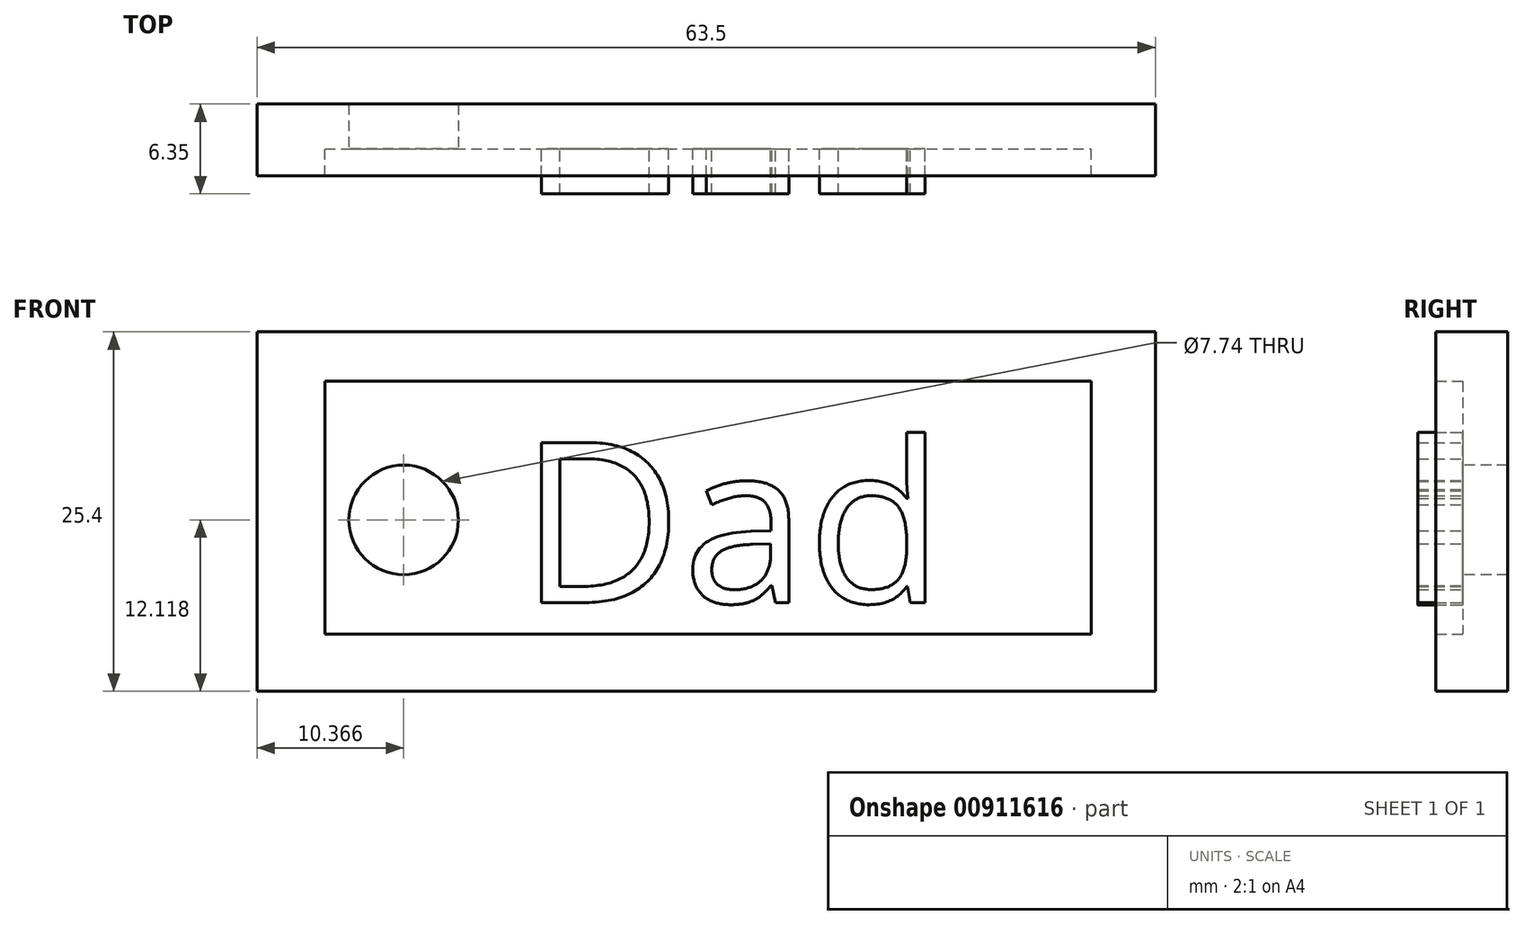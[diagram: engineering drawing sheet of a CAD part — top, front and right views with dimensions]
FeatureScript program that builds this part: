
annotation { "Feature Type Name" : "Feature", "Feature Type Description" : "" }
export const myFeature = defineFeature(function(context is Context, id is Id, definition is map)
    precondition{}
    {
        {
            var Q0;
            Q0=qCreatedBy(makeId("Front.planeOp"),FACE);
            var sketch = newSketch(context, id + "F0", { "sketchPlane" : qUnion([Q0])});
            skLineSegment(sketch, "E0.bottom", {"start": v(0, 25.4) * mm, "end": v(63.5, 25.4) * mm});
            skLineSegment(sketch, "E0.top", {"start": v(0, 0) * mm, "end": v(63.5, 0) * mm});
            skLineSegment(sketch, "E0.left", {"start": v(0, 25.4) * mm, "end": v(0, 0) * mm});
            skLineSegment(sketch, "E0.right", {"start": v(63.5, 25.4) * mm, "end": v(63.5, 0) * mm});
            skLineSegment(sketch, "E1.bottom", {"start": v(4.79, 21.92) * mm, "end": v(58.96, 21.92) * mm});
            skLineSegment(sketch, "E1.top", {"start": v(4.79, 4.05) * mm, "end": v(58.96, 4.05) * mm});
            skLineSegment(sketch, "E1.left", {"start": v(4.79, 21.92) * mm, "end": v(4.79, 4.05) * mm});
            skLineSegment(sketch, "E1.right", {"start": v(58.96, 21.92) * mm, "end": v(58.96, 4.05) * mm});
            skSolve(sketch);
        }
        {
            var Q0;
            Q0=qSketchRegion(id+"F0",true);
            extrude(context, id + "F1", {"entities" : qUnion([Q0]), "depth" : 5.08 * mm, "offsetDistance" : 25.4 * mm});
        }
        {
            var Q0;
            Q0=makeQuery(id+"F0.imprint","IMPRINT",FACE,{"disambiguationData":[TD([[makeQuery(id+"F0.imprint","IMPRINT",EDGE,{"derivedFrom":sQuery(id+"F0.wireOp",EDGE,"E1.bottom")}),-1.0]])]});
            extrude(context, id + "F2", {"entities" : qUnion([Q0]), "operationType" : NewBodyOperationType.ADD, "depth" : 3.17 * mm, "offsetDistance" : 25.4 * mm});
        }
        {
            var Q0;
            Q0=makeQuery(id+"F2.opExtrude","CAP_FACE",FACE,{"disambiguationData":[OSD([sQuery(id+"F0.wireOp",EDGE,"E1.bottom"),sQuery(id+"F0.wireOp",EDGE,"E1.top"),sQuery(id+"F0.wireOp",EDGE,"E1.left"),sQuery(id+"F0.wireOp",EDGE,"E1.right")])],"isStart":false});
            var sketch = newSketch(context, id + "F3", { "sketchPlane" : qUnion([Q0])});
            skCircle(sketch, "E2", {"center": v(10.37, 12.12) * mm, "radius": 3.87 * mm});
            skSolve(sketch);
        }
        {
            var Q0;
            Q0=qCreatedBy(makeId("Front.planeOp"),FACE);
            var sketch = newSketch(context, id + "F4", { "sketchPlane" : qUnion([Q0])});
            skText(sketch, "E3", { "text": "Dad", "fontName": "OpenSans-Regular.ttf"});
            const initialGuessF4  = {"E3": [0.01854, 0.00628, 1, 0, 0.01139]};
            skSetInitialGuess(sketch, initialGuessF4);
            skSolve(sketch);
        }
        {
            var Q0;
            Q0=qSketchRegion(id+"F4",true);
            extrude(context, id + "F5", {"entities" : qUnion([Q0]), "operationType" : NewBodyOperationType.ADD, "depth" : 6.35 * mm, "offsetDistance" : 25.4 * mm});
        }
        {
            var Q0;
            Q0=makeQuery(id+"F3.imprint","IMPRINT",FACE,{"disambiguationData":[TD([[makeQuery(id+"F3.imprint","IMPRINT",EDGE,{"derivedFrom":sQuery(id+"F3.wireOp",EDGE,"E2")}),1.0]])]});
            extrude(context, id + "F6", {"entities" : qUnion([Q0]), "operationType" : NewBodyOperationType.REMOVE, "oppositeDirection" : true, "depth" : 25.4 * mm, "offsetDistance" : 25.4 * mm});
        }
    });
